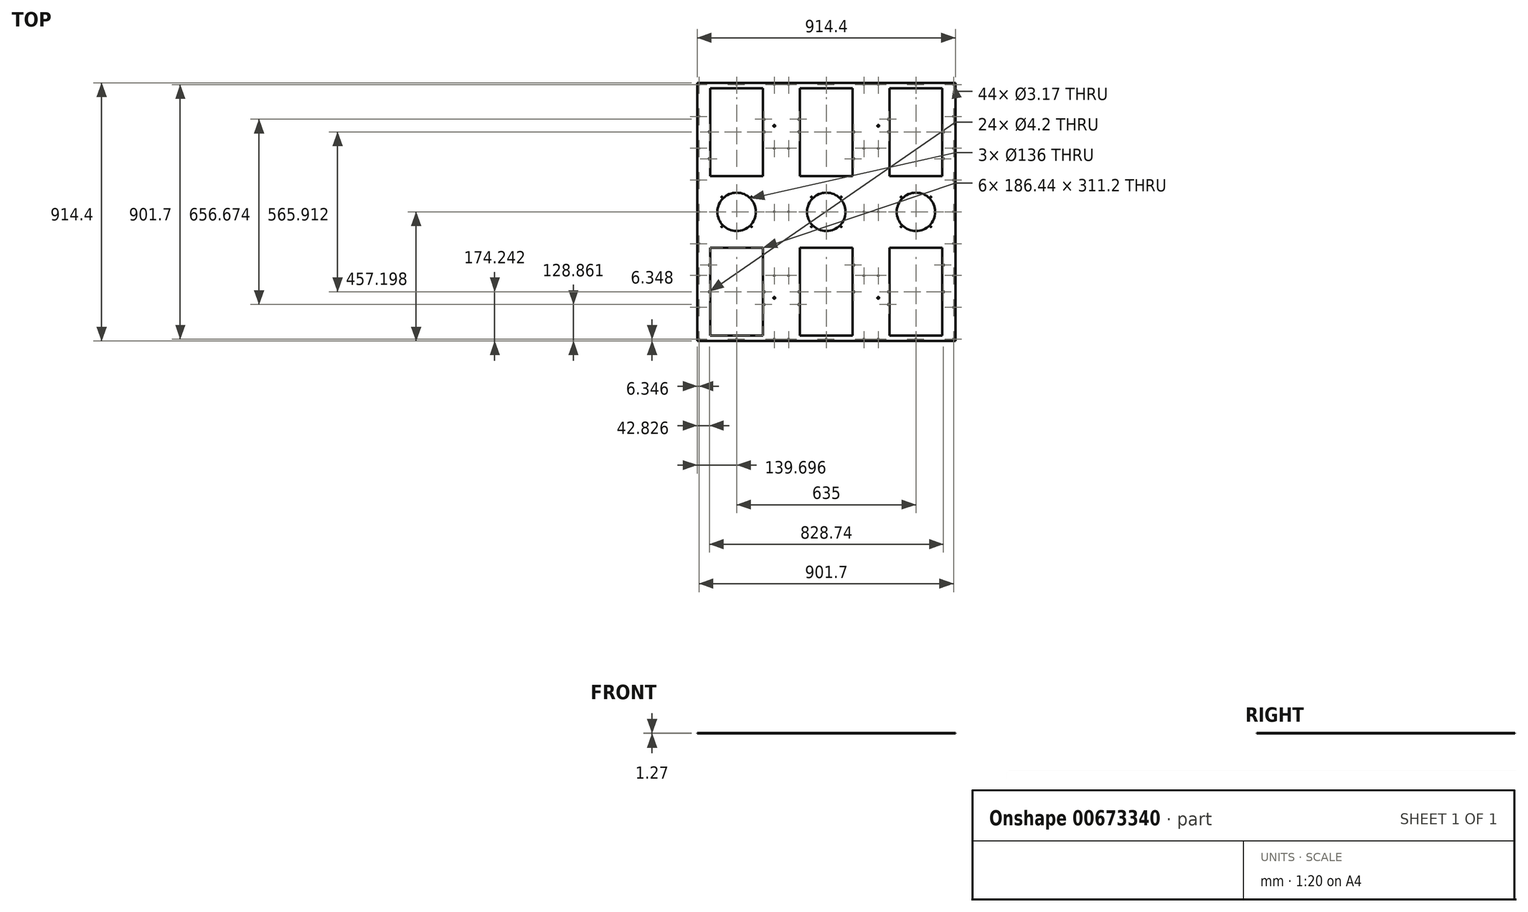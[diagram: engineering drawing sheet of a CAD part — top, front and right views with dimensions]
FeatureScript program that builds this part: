
annotation { "Feature Type Name" : "Feature", "Feature Type Description" : "" }
export const myFeature = defineFeature(function(context is Context, id is Id, definition is map)
    precondition{}
    {
        {
            var Q0;
            Q0=qCreatedBy(makeId("Top.planeOp"),FACE);
            var sketch = newSketch(context, id + "F0", { "sketchPlane" : qUnion([Q0])});
            skLineSegment(sketch, "E0.bottom", {"start": v(-471.91, 518.2) * mm, "end": v(442.49, 518.2) * mm});
            skLineSegment(sketch, "E0.top", {"start": v(-471.91, -396.2) * mm, "end": v(442.49, -396.2) * mm});
            skLineSegment(sketch, "E0.left", {"start": v(-471.91, 518.2) * mm, "end": v(-471.91, -396.2) * mm});
            skLineSegment(sketch, "E0.right", {"start": v(442.49, 518.2) * mm, "end": v(442.49, -396.2) * mm});
            skLineSegment(sketch, "E1", {"start": v(-14.71, 518.2) * mm, "end": v(-14.71, -396.2) * mm, "construction": true});
            skLineSegment(sketch, "E2", {"start": v(-471.91, 61) * mm, "end": v(442.49, 61) * mm, "construction": true});
            skLineSegment(sketch, "E3.0", {"start": v(-459.21, 505.5) * mm, "end": v(-459.21, -383.5) * mm, "construction": true});
            skLineSegment(sketch, "E4.0", {"start": v(-471.91, 505.5) * mm, "end": v(442.49, 505.5) * mm, "construction": true});
            skLineSegment(sketch, "E5.0", {"start": v(429.79, 505.5) * mm, "end": v(429.79, -383.5) * mm, "construction": true});
            skLineSegment(sketch, "E6.0", {"start": v(-471.91, -383.5) * mm, "end": v(442.49, -383.5) * mm, "construction": true});
            skLineSegment(sketch, "E7.0", {"start": v(-192.51, 505.5) * mm, "end": v(-192.51, -383.5) * mm, "construction": true});
            skLineSegment(sketch, "E8.0", {"start": v(-205.21, 505.5) * mm, "end": v(-205.21, -383.5) * mm, "construction": true});
            skLineSegment(sketch, "E9.0", {"start": v(-154.41, 505.5) * mm, "end": v(-154.41, -383.5) * mm, "construction": true});
            skLineSegment(sketch, "E10.0", {"start": v(124.99, 505.5) * mm, "end": v(124.99, -383.5) * mm, "construction": true});
            skLineSegment(sketch, "E11.0", {"start": v(163.09, 505.5) * mm, "end": v(163.09, -383.5) * mm, "construction": true});
            skLineSegment(sketch, "E12.0", {"start": v(175.79, 505.5) * mm, "end": v(175.79, -383.5) * mm, "construction": true});
            skLineSegment(sketch, "E13.0", {"start": v(-141.71, 505.5) * mm, "end": v(-141.71, -383.5) * mm, "construction": true});
            skLineSegment(sketch, "E14.0", {"start": v(112.29, 505.5) * mm, "end": v(112.29, -383.5) * mm, "construction": true});
            skLineSegment(sketch, "E15.0", {"start": v(-332.21, 505.5) * mm, "end": v(-332.21, -383.5) * mm, "construction": true});
            skLineSegment(sketch, "E16.0", {"start": v(302.79, 505.5) * mm, "end": v(302.79, -383.5) * mm, "construction": true});
            skPoint(sketch, "E17.middle", {"position": v(-332.21, 61) * mm});
            skCircle(sketch, "E18", {"center": v(-332.21, 61) * mm, "radius": 68 * mm});
            skCircle(sketch, "E19", {"center": v(-384.71, 113.5) * mm, "radius": 1.65 * mm});
            skCircle(sketch, "E20.MirrorC", {"center": v(-279.71, 113.5) * mm, "radius": 1.65 * mm});
            skCircle(sketch, "E21.MirrorC", {"center": v(-384.71, 8.5) * mm, "radius": 1.65 * mm});
            skCircle(sketch, "E22.MirrorC", {"center": v(-279.71, 8.5) * mm, "radius": 1.65 * mm});
            skCircle(sketch, "E23.MirrorC", {"center": v(250.29, 113.5) * mm, "radius": 1.65 * mm});
            skCircle(sketch, "E24.MirrorC", {"center": v(355.29, 113.5) * mm, "radius": 1.65 * mm});
            skCircle(sketch, "E25.MirrorC", {"center": v(355.29, 8.5) * mm, "radius": 1.65 * mm});
            skCircle(sketch, "E26.MirrorC", {"center": v(250.29, 8.5) * mm, "radius": 1.65 * mm});
            skCircle(sketch, "E27.MirrorC", {"center": v(302.79, 61) * mm, "radius": 68 * mm});
            skCircle(sketch, "E28.MirrorC", {"center": v(-14.71, 61) * mm, "radius": 68 * mm});
            skCircle(sketch, "E29.MirrorC", {"center": v(-67.21, 113.5) * mm, "radius": 1.65 * mm});
            skCircle(sketch, "E30.MirrorC", {"center": v(37.79, 113.5) * mm, "radius": 1.65 * mm});
            skCircle(sketch, "E31.MirrorC", {"center": v(37.79, 8.5) * mm, "radius": 1.65 * mm});
            skCircle(sketch, "E32.MirrorC", {"center": v(-67.21, 8.5) * mm, "radius": 1.65 * mm});
            skLineSegment(sketch, "E33.left", {"start": v(-435.08, 499.15) * mm, "end": v(-435.08, 188.76) * mm, "construction": true});
            skLineSegment(sketch, "E33.right", {"start": v(-229.34, 499.15) * mm, "end": v(-229.34, 188.76) * mm, "construction": true});
            skLineSegment(sketch, "E34.MirrorCS", {"start": v(-117.58, 499.15) * mm, "end": v(-117.58, 188.76) * mm, "construction": true});
            skLineSegment(sketch, "E35.MirrorCS", {"start": v(88.16, 499.15) * mm, "end": v(88.16, 188.76) * mm, "construction": true});
            skLineSegment(sketch, "E36.MirrorCS", {"start": v(199.92, 499.15) * mm, "end": v(199.92, 188.76) * mm, "construction": true});
            skLineSegment(sketch, "E37.MirrorCS", {"start": v(405.66, 499.15) * mm, "end": v(405.66, 188.76) * mm, "construction": true});
            skLineSegment(sketch, "E38.MirrorCS", {"start": v(-435.08, -377.15) * mm, "end": v(-435.08, -66.76) * mm, "construction": true});
            skLineSegment(sketch, "E39.MirrorCS", {"start": v(-229.34, -377.15) * mm, "end": v(-229.34, -66.76) * mm, "construction": true});
            skLineSegment(sketch, "E40.MirrorCS", {"start": v(-117.58, -377.15) * mm, "end": v(-117.58, -66.76) * mm, "construction": true});
            skLineSegment(sketch, "E41.MirrorCS", {"start": v(88.16, -377.15) * mm, "end": v(88.16, -66.76) * mm, "construction": true});
            skLineSegment(sketch, "E42.MirrorCS", {"start": v(199.92, -377.15) * mm, "end": v(199.92, -66.76) * mm, "construction": true});
            skLineSegment(sketch, "E43.MirrorCS", {"start": v(405.66, -377.15) * mm, "end": v(405.66, -66.76) * mm, "construction": true});
            skLineSegment(sketch, "E44.bottom", {"start": v(-419, 486.96) * mm, "end": v(-245.42, 486.96) * mm, "construction": true});
            skLineSegment(sketch, "E44.top", {"start": v(-419, 200.95) * mm, "end": v(-245.42, 200.95) * mm, "construction": true});
            skLineSegment(sketch, "E44.left", {"start": v(-419, 486.96) * mm, "end": v(-419, 200.95) * mm, "construction": true});
            skLineSegment(sketch, "E44.right", {"start": v(-245.42, 486.96) * mm, "end": v(-245.42, 200.95) * mm, "construction": true});
            skLineSegment(sketch, "E45.MirrorCS", {"start": v(-101.5, 486.96) * mm, "end": v(-101.5, 200.95) * mm, "construction": true});
            skLineSegment(sketch, "E46.MirrorCS", {"start": v(72.08, 486.96) * mm, "end": v(-101.5, 486.96) * mm, "construction": true});
            skLineSegment(sketch, "E47.MirrorCS", {"start": v(72.08, 486.96) * mm, "end": v(72.08, 200.95) * mm, "construction": true});
            skLineSegment(sketch, "E48.MirrorCS", {"start": v(72.08, 200.95) * mm, "end": v(-101.5, 200.95) * mm, "construction": true});
            skLineSegment(sketch, "E49.MirrorCS", {"start": v(216, 486.96) * mm, "end": v(216, 200.95) * mm, "construction": true});
            skLineSegment(sketch, "E50.MirrorCS", {"start": v(389.58, 486.96) * mm, "end": v(216, 486.96) * mm, "construction": true});
            skLineSegment(sketch, "E51.MirrorCS", {"start": v(389.58, 200.95) * mm, "end": v(216, 200.95) * mm, "construction": true});
            skLineSegment(sketch, "E52.MirrorCS", {"start": v(389.58, 486.96) * mm, "end": v(389.58, 200.95) * mm, "construction": true});
            skLineSegment(sketch, "E53.MirrorCS", {"start": v(-419, -78.96) * mm, "end": v(-245.42, -78.96) * mm, "construction": true});
            skLineSegment(sketch, "E54.MirrorCS", {"start": v(-245.42, -364.96) * mm, "end": v(-245.42, -78.96) * mm, "construction": true});
            skLineSegment(sketch, "E55.MirrorCS", {"start": v(-419, -364.96) * mm, "end": v(-419, -78.96) * mm, "construction": true});
            skLineSegment(sketch, "E56.MirrorCS", {"start": v(-419, -364.96) * mm, "end": v(-245.42, -364.96) * mm, "construction": true});
            skLineSegment(sketch, "E57.MirrorCS", {"start": v(72.08, -364.96) * mm, "end": v(-101.5, -364.96) * mm, "construction": true});
            skLineSegment(sketch, "E58.MirrorCS", {"start": v(-101.5, -364.96) * mm, "end": v(-101.5, -78.96) * mm, "construction": true});
            skLineSegment(sketch, "E59.MirrorCS", {"start": v(72.08, -78.96) * mm, "end": v(-101.5, -78.96) * mm, "construction": true});
            skLineSegment(sketch, "E60.MirrorCS", {"start": v(72.08, -364.96) * mm, "end": v(72.08, -78.96) * mm, "construction": true});
            skLineSegment(sketch, "E61.MirrorCS", {"start": v(216, -364.96) * mm, "end": v(216, -78.96) * mm, "construction": true});
            skLineSegment(sketch, "E62.MirrorCS", {"start": v(389.58, -364.96) * mm, "end": v(216, -364.96) * mm, "construction": true});
            skLineSegment(sketch, "E63.MirrorCS", {"start": v(389.58, -364.96) * mm, "end": v(389.58, -78.96) * mm, "construction": true});
            skLineSegment(sketch, "E64.MirrorCS", {"start": v(389.58, -78.96) * mm, "end": v(216, -78.96) * mm, "construction": true});
            skCircle(sketch, "E65", {"center": v(-332.21, 141.14) * mm, "radius": 9.53 * mm, "construction": true});
            skCircle(sketch, "E66", {"center": v(-245.42, 172.89) * mm, "radius": 9.53 * mm, "construction": true});
            skCircle(sketch, "E67", {"center": v(-419, 172.89) * mm, "radius": 9.53 * mm, "construction": true});
            skCircle(sketch, "E68.MirrorC", {"center": v(216, 172.89) * mm, "radius": 9.53 * mm, "construction": true});
            skCircle(sketch, "E69.MirrorC", {"center": v(302.79, 141.14) * mm, "radius": 9.53 * mm, "construction": true});
            skCircle(sketch, "E70.MirrorC", {"center": v(389.58, 172.89) * mm, "radius": 9.53 * mm, "construction": true});
            skCircle(sketch, "E71.MirrorC", {"center": v(-245.42, -50.89) * mm, "radius": 9.53 * mm, "construction": true});
            skCircle(sketch, "E72.MirrorC", {"center": v(-332.21, -19.14) * mm, "radius": 9.53 * mm, "construction": true});
            skCircle(sketch, "E73.MirrorC", {"center": v(-419, -50.89) * mm, "radius": 9.53 * mm, "construction": true});
            skCircle(sketch, "E74.MirrorC", {"center": v(216, -50.89) * mm, "radius": 9.53 * mm, "construction": true});
            skCircle(sketch, "E75.MirrorC", {"center": v(302.79, -19.14) * mm, "radius": 9.53 * mm, "construction": true});
            skCircle(sketch, "E76.MirrorC", {"center": v(389.58, -50.89) * mm, "radius": 9.53 * mm, "construction": true});
            skCircle(sketch, "E77", {"center": v(-447.15, -196.18) * mm, "radius": 9.53 * mm, "construction": true});
            skCircle(sketch, "E78", {"center": v(-447.15, -348.58) * mm, "radius": 9.53 * mm, "construction": true});
            skCircle(sketch, "E79.MirrorC", {"center": v(-217.28, -196.18) * mm, "radius": 9.53 * mm, "construction": true});
            skCircle(sketch, "E80.MirrorC", {"center": v(-217.28, -348.58) * mm, "radius": 9.53 * mm, "construction": true});
            skCircle(sketch, "E81.MirrorC", {"center": v(187.85, -196.18) * mm, "radius": 9.53 * mm, "construction": true});
            skCircle(sketch, "E82.MirrorC", {"center": v(187.85, -348.58) * mm, "radius": 9.53 * mm, "construction": true});
            skCircle(sketch, "E83.MirrorC", {"center": v(417.72, -196.18) * mm, "radius": 9.53 * mm, "construction": true});
            skCircle(sketch, "E84.MirrorC", {"center": v(417.72, -348.58) * mm, "radius": 9.53 * mm, "construction": true});
            skCircle(sketch, "E85.MirrorC", {"center": v(-447.15, 318.17) * mm, "radius": 9.53 * mm, "construction": true});
            skCircle(sketch, "E86.MirrorC", {"center": v(-447.15, 470.57) * mm, "radius": 9.53 * mm, "construction": true});
            skCircle(sketch, "E87.MirrorC", {"center": v(-217.28, 318.17) * mm, "radius": 9.53 * mm, "construction": true});
            skCircle(sketch, "E88.MirrorC", {"center": v(-217.28, 470.57) * mm, "radius": 9.53 * mm, "construction": true});
            skCircle(sketch, "E89.MirrorC", {"center": v(187.85, 470.57) * mm, "radius": 9.53 * mm, "construction": true});
            skCircle(sketch, "E90.MirrorC", {"center": v(187.85, 318.17) * mm, "radius": 9.53 * mm, "construction": true});
            skCircle(sketch, "E91.MirrorC", {"center": v(417.72, 318.17) * mm, "radius": 9.53 * mm, "construction": true});
            skCircle(sketch, "E92.MirrorC", {"center": v(417.72, 470.57) * mm, "radius": 9.53 * mm, "construction": true});
            skCircle(sketch, "E93.MirrorC", {"center": v(-129.65, 470.57) * mm, "radius": 9.53 * mm, "construction": true});
            skCircle(sketch, "E94.MirrorC", {"center": v(100.22, 470.57) * mm, "radius": 9.53 * mm, "construction": true});
            skCircle(sketch, "E95.MirrorC", {"center": v(100.22, 318.17) * mm, "radius": 9.53 * mm, "construction": true});
            skCircle(sketch, "E96.MirrorC", {"center": v(-129.65, 318.17) * mm, "radius": 9.53 * mm, "construction": true});
            skCircle(sketch, "E97.MirrorC", {"center": v(-101.5, 172.89) * mm, "radius": 9.53 * mm, "construction": true});
            skCircle(sketch, "E98.MirrorC", {"center": v(-14.71, 141.14) * mm, "radius": 9.53 * mm, "construction": true});
            skCircle(sketch, "E99.MirrorC", {"center": v(72.08, 172.89) * mm, "radius": 9.53 * mm, "construction": true});
            skCircle(sketch, "E100.MirrorC", {"center": v(72.08, -50.89) * mm, "radius": 9.53 * mm, "construction": true});
            skCircle(sketch, "E101.MirrorC", {"center": v(-14.71, -19.14) * mm, "radius": 9.53 * mm, "construction": true});
            skCircle(sketch, "E102.MirrorC", {"center": v(-101.5, -50.89) * mm, "radius": 9.53 * mm, "construction": true});
            skCircle(sketch, "E103.MirrorC", {"center": v(-129.65, -196.18) * mm, "radius": 9.53 * mm, "construction": true});
            skCircle(sketch, "E104.MirrorC", {"center": v(-129.65, -348.58) * mm, "radius": 9.53 * mm, "construction": true});
            skCircle(sketch, "E105.MirrorC", {"center": v(100.22, -348.58) * mm, "radius": 9.53 * mm, "construction": true});
            skCircle(sketch, "E106.MirrorC", {"center": v(100.22, -196.18) * mm, "radius": 9.53 * mm, "construction": true});
            skCircle(sketch, "E107", {"center": v(-447.15, 61) * mm, "radius": 9.53 * mm, "construction": true});
            skCircle(sketch, "E108", {"center": v(417.72, 61) * mm, "radius": 9.53 * mm, "construction": true});
            skCircle(sketch, "E109", {"center": v(436.14, 511.85) * mm, "radius": 1.59 * mm});
            skCircle(sketch, "E110", {"center": v(302.79, 511.85) * mm, "radius": 1.59 * mm});
            skLineSegment(sketch, "E111", {"start": v(169.44, 505.5) * mm, "end": v(169.44, 518.2) * mm, "construction": true});
            skCircle(sketch, "E112", {"center": v(169.44, 511.85) * mm, "radius": 1.59 * mm});
            skCircle(sketch, "E113", {"center": v(436.14, 61) * mm, "radius": 1.59 * mm});
            skCircle(sketch, "E114", {"center": v(436.14, 399.14) * mm, "radius": 1.59 * mm});
            skCircle(sketch, "E115", {"center": v(436.14, 286.42) * mm, "radius": 1.59 * mm});
            skCircle(sketch, "E116", {"center": v(436.14, 173.71) * mm, "radius": 1.59 * mm});
            skCircle(sketch, "E117.MirrorC", {"center": v(169.44, 286.42) * mm, "radius": 1.59 * mm});
            skCircle(sketch, "E118.MirrorC", {"center": v(169.44, 61) * mm, "radius": 1.59 * mm});
            skCircle(sketch, "E119.MirrorC", {"center": v(169.44, -164.43) * mm, "radius": 1.59 * mm});
            skCircle(sketch, "E120.MirrorC", {"center": v(169.44, -389.85) * mm, "radius": 1.59 * mm});
            skCircle(sketch, "E121.MirrorC", {"center": v(302.79, -389.85) * mm, "radius": 1.59 * mm});
            skCircle(sketch, "E122.MirrorC", {"center": v(436.14, -389.85) * mm, "radius": 1.59 * mm});
            skCircle(sketch, "E123.MirrorC", {"center": v(436.14, -277.14) * mm, "radius": 1.59 * mm});
            skCircle(sketch, "E124.MirrorC", {"center": v(436.14, -164.43) * mm, "radius": 1.59 * mm});
            skCircle(sketch, "E125.MirrorC", {"center": v(436.14, -51.71) * mm, "radius": 1.59 * mm});
            skCircle(sketch, "E126.MirrorC", {"center": v(-198.86, 61) * mm, "radius": 1.59 * mm});
            skCircle(sketch, "E127.MirrorC", {"center": v(-198.86, 286.42) * mm, "radius": 1.59 * mm});
            skCircle(sketch, "E128.MirrorC", {"center": v(-198.86, 511.85) * mm, "radius": 1.59 * mm});
            skCircle(sketch, "E129.MirrorC", {"center": v(-332.21, 511.85) * mm, "radius": 1.59 * mm});
            skCircle(sketch, "E130.MirrorC", {"center": v(-465.56, 511.85) * mm, "radius": 1.59 * mm});
            skCircle(sketch, "E131.MirrorC", {"center": v(-465.56, 399.14) * mm, "radius": 1.59 * mm});
            skCircle(sketch, "E132.MirrorC", {"center": v(-465.56, 286.42) * mm, "radius": 1.59 * mm});
            skCircle(sketch, "E133.MirrorC", {"center": v(-465.56, 173.71) * mm, "radius": 1.59 * mm});
            skCircle(sketch, "E134.MirrorC", {"center": v(-465.56, 61) * mm, "radius": 1.59 * mm});
            skCircle(sketch, "E135.MirrorC", {"center": v(-465.56, -51.71) * mm, "radius": 1.59 * mm});
            skCircle(sketch, "E136.MirrorC", {"center": v(-465.56, -164.43) * mm, "radius": 1.59 * mm});
            skCircle(sketch, "E137.MirrorC", {"center": v(-465.56, -277.14) * mm, "radius": 1.59 * mm});
            skCircle(sketch, "E138.MirrorC", {"center": v(-465.56, -389.85) * mm, "radius": 1.59 * mm});
            skCircle(sketch, "E139.MirrorC", {"center": v(-332.21, -389.85) * mm, "radius": 1.59 * mm});
            skCircle(sketch, "E140.MirrorC", {"center": v(-198.86, -389.85) * mm, "radius": 1.59 * mm});
            skCircle(sketch, "E141.MirrorC", {"center": v(-198.86, -164.43) * mm, "radius": 1.59 * mm});
            skCircle(sketch, "E142.MirrorC", {"center": v(118.64, 61) * mm, "radius": 1.59 * mm});
            skCircle(sketch, "E143.MirrorC", {"center": v(118.64, 286.42) * mm, "radius": 1.59 * mm});
            skCircle(sketch, "E144.MirrorC", {"center": v(118.64, 511.85) * mm, "radius": 1.59 * mm});
            skCircle(sketch, "E145.MirrorC", {"center": v(-14.71, 511.85) * mm, "radius": 1.59 * mm});
            skCircle(sketch, "E146.MirrorC", {"center": v(-148.06, 511.85) * mm, "radius": 1.59 * mm});
            skCircle(sketch, "E147.MirrorC", {"center": v(-148.06, 286.42) * mm, "radius": 1.59 * mm});
            skCircle(sketch, "E148.MirrorC", {"center": v(-148.06, 61) * mm, "radius": 1.59 * mm});
            skCircle(sketch, "E149.MirrorC", {"center": v(-148.06, -164.43) * mm, "radius": 1.59 * mm});
            skCircle(sketch, "E150.MirrorC", {"center": v(-148.06, -389.85) * mm, "radius": 1.59 * mm});
            skCircle(sketch, "E151.MirrorC", {"center": v(-14.71, -389.85) * mm, "radius": 1.59 * mm});
            skCircle(sketch, "E152.MirrorC", {"center": v(118.64, -389.85) * mm, "radius": 1.59 * mm});
            skCircle(sketch, "E153.MirrorC", {"center": v(118.64, -164.43) * mm, "radius": 1.59 * mm});
            skCircle(sketch, "E154", {"center": v(169.44, 365.8) * mm, "radius": 3.15 * mm});
            skCircle(sketch, "E155.MirrorC", {"center": v(-198.86, 365.8) * mm, "radius": 3.15 * mm});
            skCircle(sketch, "E156.MirrorC", {"center": v(-198.86, -243.8) * mm, "radius": 3.15 * mm});
            skCircle(sketch, "E157.MirrorC", {"center": v(169.44, -243.8) * mm, "radius": 3.15 * mm});
            skCircle(sketch, "E158", {"center": v(-111.58, 344.34) * mm, "radius": 2.1 * mm});
            skCircle(sketch, "E159.MirrorC", {"center": v(82.16, 344.34) * mm, "radius": 2.1 * mm});
            skCircle(sketch, "E160", {"center": v(-111.58, 389.34) * mm, "radius": 2.1 * mm});
            skCircle(sketch, "E161.MirrorC", {"center": v(82.16, 249.34) * mm, "radius": 2.1 * mm});
            skLineSegment(sketch, "E162.0", {"start": v(-173.46, 505.5) * mm, "end": v(-173.46, -383.5) * mm});
            skCircle(sketch, "E163.MirrorC", {"center": v(-429.08, 344.34) * mm, "radius": 2.1 * mm});
            skCircle(sketch, "E164.MirrorC", {"center": v(-429.08, 249.34) * mm, "radius": 2.1 * mm});
            skCircle(sketch, "E165.MirrorC", {"center": v(-235.34, 344.34) * mm, "radius": 2.1 * mm});
            skCircle(sketch, "E166.MirrorC", {"center": v(-235.34, 389.34) * mm, "radius": 2.1 * mm});
            skLineSegment(sketch, "E167.MirrorCS", {"start": v(209.57, 499.15) * mm, "end": v(209.57, 188.76) * mm});
            skLineSegment(sketch, "E168.MirrorCS", {"start": v(396, 499.15) * mm, "end": v(396, 188.76) * mm});
            skCircle(sketch, "E169.MirrorC", {"center": v(399.66, 344.34) * mm, "radius": 2.1 * mm});
            skCircle(sketch, "E170.MirrorC", {"center": v(399.66, 249.34) * mm, "radius": 2.1 * mm});
            skCircle(sketch, "E171.MirrorC", {"center": v(205.92, 344.34) * mm, "radius": 2.1 * mm});
            skCircle(sketch, "E172.MirrorC", {"center": v(205.92, 389.34) * mm, "radius": 2.1 * mm});
            skCircle(sketch, "E173.MirrorC", {"center": v(-429.08, -127.34) * mm, "radius": 2.1 * mm});
            skCircle(sketch, "E174.MirrorC", {"center": v(-429.08, -222.34) * mm, "radius": 2.1 * mm});
            skCircle(sketch, "E175.MirrorC", {"center": v(-235.34, -222.34) * mm, "radius": 2.1 * mm});
            skCircle(sketch, "E176.MirrorC", {"center": v(-235.34, -267.34) * mm, "radius": 2.1 * mm});
            skCircle(sketch, "E177.MirrorC", {"center": v(-111.58, -267.34) * mm, "radius": 2.1 * mm});
            skCircle(sketch, "E178.MirrorC", {"center": v(-111.58, -222.34) * mm, "radius": 2.1 * mm});
            skCircle(sketch, "E179.MirrorC", {"center": v(82.16, -222.34) * mm, "radius": 2.1 * mm});
            skCircle(sketch, "E180.MirrorC", {"center": v(82.16, -127.34) * mm, "radius": 2.1 * mm});
            skCircle(sketch, "E181.MirrorC", {"center": v(205.92, -267.34) * mm, "radius": 2.1 * mm});
            skCircle(sketch, "E182.MirrorC", {"center": v(205.92, -222.34) * mm, "radius": 2.1 * mm});
            skCircle(sketch, "E183.MirrorC", {"center": v(399.66, -222.34) * mm, "radius": 2.1 * mm});
            skCircle(sketch, "E184.MirrorC", {"center": v(399.66, -127.34) * mm, "radius": 2.1 * mm});
            skPoint(sketch, "E185.orphan", {"position": v(199.92, -66.76) * mm});
            skPoint(sketch, "E186.orphan", {"position": v(199.92, -377.15) * mm});
            skPoint(sketch, "E187.orphan", {"position": v(405.66, -377.15) * mm});
            skPoint(sketch, "E188.orphan", {"position": v(405.66, -66.76) * mm});
            skPoint(sketch, "E189.orphan", {"position": v(-117.58, -377.15) * mm});
            skPoint(sketch, "E190.orphan", {"position": v(88.16, -377.15) * mm});
            skPoint(sketch, "E191.orphan", {"position": v(-229.34, -66.76) * mm});
            skPoint(sketch, "E192.orphan", {"position": v(-229.34, -377.15) * mm});
            skPoint(sketch, "E193.orphan", {"position": v(-435.08, -377.15) * mm});
            skPoint(sketch, "E194.orphan", {"position": v(-435.08, -66.76) * mm});
            skPoint(sketch, "E195.orphan", {"position": v(-117.58, 499.15) * mm});
            skPoint(sketch, "E196.orphan", {"position": v(88.16, 499.15) * mm});
            skPoint(sketch, "E197.orphan", {"position": v(199.92, 188.76) * mm});
            skPoint(sketch, "E198.orphan", {"position": v(405.66, 188.76) * mm});
            skPoint(sketch, "E199.orphan", {"position": v(405.66, 499.15) * mm});
            skPoint(sketch, "E200.orphan", {"position": v(199.92, 499.15) * mm});
            skLineSegment(sketch, "E201.0", {"start": v(396, 499.55) * mm, "end": v(209.57, 499.55) * mm});
            skLineSegment(sketch, "E202.0", {"start": v(396, 188.35) * mm, "end": v(209.57, 188.35) * mm});
            skLineSegment(sketch, "E203", {"start": v(396, 499.15) * mm, "end": v(396, 499.55) * mm});
            skLineSegment(sketch, "E204", {"start": v(396, 188.76) * mm, "end": v(396, 188.35) * mm});
            skLineSegment(sketch, "E205", {"start": v(209.57, 188.76) * mm, "end": v(209.57, 188.35) * mm});
            skLineSegment(sketch, "E206", {"start": v(209.57, 499.55) * mm, "end": v(209.57, 499.15) * mm});
            skLineSegment(sketch, "E207.MirrorCS", {"start": v(-239, 499.15) * mm, "end": v(-239, 188.76) * mm});
            skLineSegment(sketch, "E208.MirrorCS", {"start": v(-425.43, 499.55) * mm, "end": v(-239, 499.55) * mm});
            skLineSegment(sketch, "E209.MirrorCS", {"start": v(-425.43, 499.15) * mm, "end": v(-425.43, 188.76) * mm});
            skLineSegment(sketch, "E210.MirrorCS", {"start": v(-425.43, 188.35) * mm, "end": v(-239, 188.35) * mm});
            skLineSegment(sketch, "E211.0", {"start": v(144.04, 505.5) * mm, "end": v(144.04, -383.5) * mm});
            skLineSegment(sketch, "E212.MirrorCS", {"start": v(78.5, 499.15) * mm, "end": v(78.5, 188.76) * mm});
            skLineSegment(sketch, "E213.MirrorCS", {"start": v(-107.93, 499.55) * mm, "end": v(78.5, 499.55) * mm});
            skLineSegment(sketch, "E214.MirrorCS", {"start": v(-107.93, 499.15) * mm, "end": v(-107.93, 188.76) * mm});
            skLineSegment(sketch, "E215.MirrorCS", {"start": v(-107.93, 188.35) * mm, "end": v(78.5, 188.35) * mm});
            skLineSegment(sketch, "E216.MirrorCS", {"start": v(-107.93, -66.36) * mm, "end": v(78.5, -66.36) * mm});
            skLineSegment(sketch, "E217.MirrorCS", {"start": v(-107.93, -377.15) * mm, "end": v(-107.93, -66.76) * mm});
            skLineSegment(sketch, "E218.MirrorCS", {"start": v(78.5, -377.15) * mm, "end": v(78.5, -66.76) * mm});
            skLineSegment(sketch, "E219.MirrorCS", {"start": v(209.57, -377.15) * mm, "end": v(209.57, -66.76) * mm});
            skLineSegment(sketch, "E220.MirrorCS", {"start": v(396, -377.15) * mm, "end": v(396, -66.76) * mm});
            skLineSegment(sketch, "E221.MirrorCS", {"start": v(396, -66.36) * mm, "end": v(209.57, -66.36) * mm});
            skLineSegment(sketch, "E222.MirrorCS", {"start": v(396, -377.56) * mm, "end": v(209.57, -377.56) * mm});
            skLineSegment(sketch, "E223.MirrorCS", {"start": v(-239, -377.15) * mm, "end": v(-239, -66.76) * mm});
            skLineSegment(sketch, "E224.MirrorCS", {"start": v(-425.43, -66.36) * mm, "end": v(-239, -66.36) * mm});
            skLineSegment(sketch, "E225.MirrorCS", {"start": v(-425.43, -377.15) * mm, "end": v(-425.43, -66.76) * mm});
            skLineSegment(sketch, "E226.MirrorCS", {"start": v(-425.43, -377.56) * mm, "end": v(-239, -377.56) * mm});
            skLineSegment(sketch, "E227.MirrorCS", {"start": v(-107.93, -377.56) * mm, "end": v(78.5, -377.56) * mm});
            skLineSegment(sketch, "E228", {"start": v(-425.43, 499.55) * mm, "end": v(-425.43, 499.15) * mm});
            skLineSegment(sketch, "E229", {"start": v(-239, 499.55) * mm, "end": v(-239, 499.15) * mm});
            skLineSegment(sketch, "E230", {"start": v(-239, 188.76) * mm, "end": v(-239, 188.35) * mm});
            skLineSegment(sketch, "E231", {"start": v(-425.43, 188.76) * mm, "end": v(-425.43, 188.35) * mm});
            skLineSegment(sketch, "E232", {"start": v(-107.93, 188.76) * mm, "end": v(-107.93, 188.35) * mm});
            skLineSegment(sketch, "E233", {"start": v(78.5, 188.76) * mm, "end": v(78.5, 188.35) * mm});
            skLineSegment(sketch, "E234", {"start": v(78.5, 499.55) * mm, "end": v(78.5, 499.15) * mm});
            skLineSegment(sketch, "E235", {"start": v(-107.93, 499.55) * mm, "end": v(-107.93, 499.15) * mm});
            skLineSegment(sketch, "E236", {"start": v(209.57, -66.36) * mm, "end": v(209.57, -66.76) * mm});
            skLineSegment(sketch, "E237", {"start": v(396, -66.36) * mm, "end": v(396, -66.76) * mm});
            skLineSegment(sketch, "E238", {"start": v(396, -377.15) * mm, "end": v(396, -377.56) * mm});
            skLineSegment(sketch, "E239", {"start": v(209.57, -377.15) * mm, "end": v(209.57, -377.56) * mm});
            skLineSegment(sketch, "E240", {"start": v(78.5, -377.15) * mm, "end": v(78.5, -377.56) * mm});
            skLineSegment(sketch, "E241", {"start": v(-107.93, -377.15) * mm, "end": v(-107.93, -377.56) * mm});
            skLineSegment(sketch, "E242", {"start": v(-107.93, -66.36) * mm, "end": v(-107.93, -66.76) * mm});
            skLineSegment(sketch, "E243", {"start": v(78.5, -66.36) * mm, "end": v(78.5, -66.76) * mm});
            skLineSegment(sketch, "E244", {"start": v(-239, -66.36) * mm, "end": v(-239, -66.76) * mm});
            skLineSegment(sketch, "E245", {"start": v(-425.43, -66.36) * mm, "end": v(-425.43, -66.76) * mm});
            skLineSegment(sketch, "E246", {"start": v(-425.43, -377.15) * mm, "end": v(-425.43, -377.56) * mm});
            skLineSegment(sketch, "E247", {"start": v(-239, -377.15) * mm, "end": v(-239, -377.56) * mm});
            skSolve(sketch);
        }
        {
            var Q0;
            Q0=makeQuery(id+"F0.imprint","IMPRINT",FACE,{"disambiguationData":[TD([[makeQuery(id+"F0.imprint","IMPRINT",EDGE,{"derivedFrom":sQuery(id+"F0.wireOp",EDGE,"E0.bottom")}),-1.0]])]});
            extrude(context, id + "F1", {"entities" : qUnion([Q0]), "depth" : 1.27 * mm, "offsetDistance" : 25.4 * mm});
        }
    });
